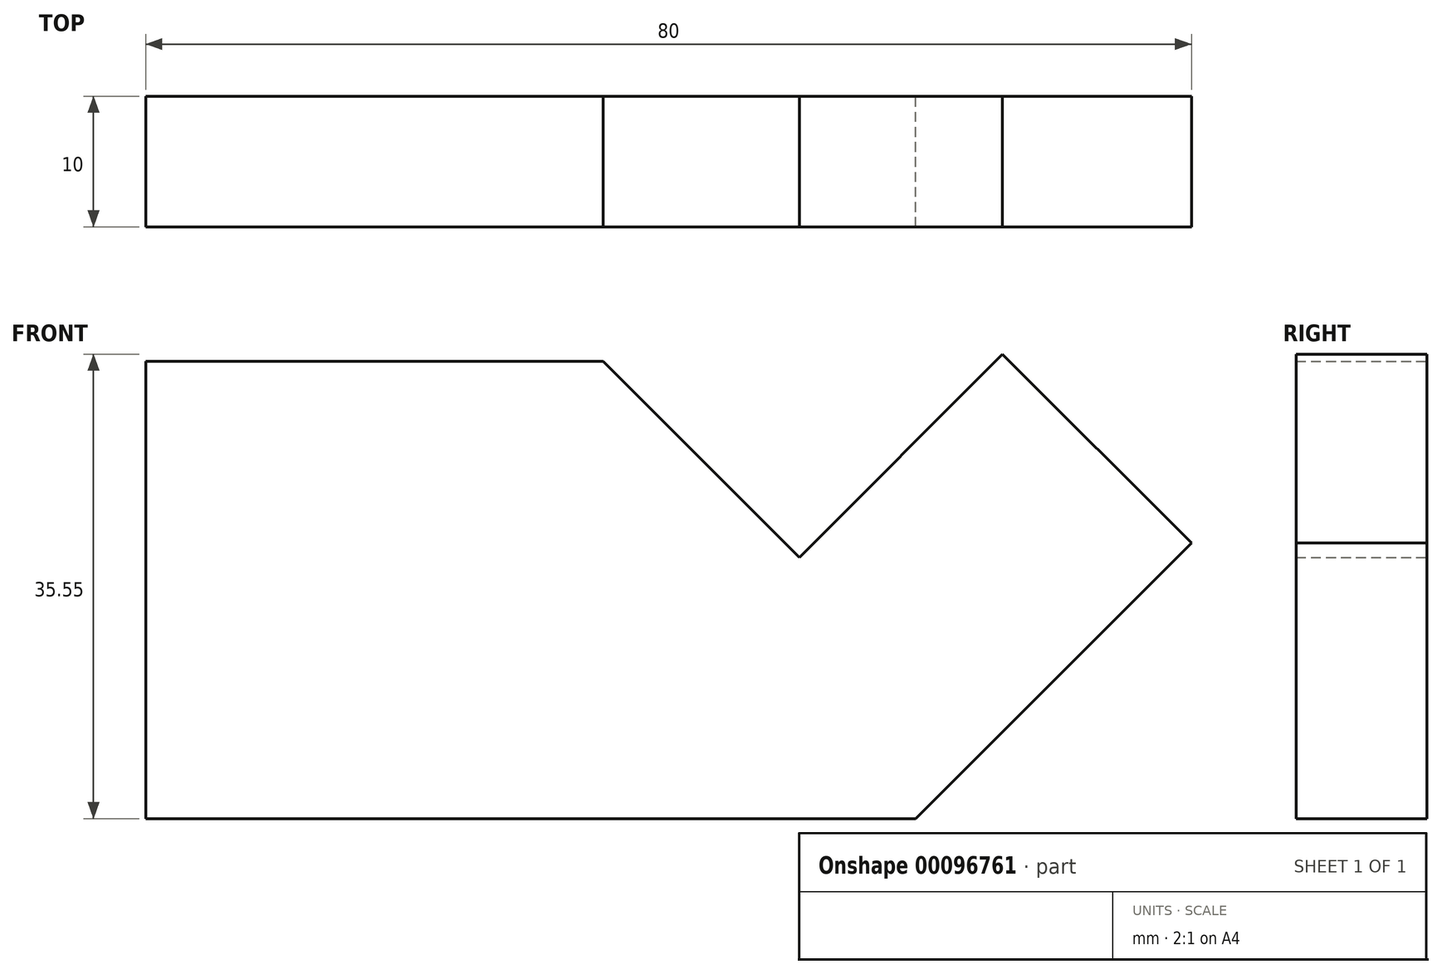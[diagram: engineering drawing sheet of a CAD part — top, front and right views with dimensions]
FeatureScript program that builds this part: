
annotation { "Feature Type Name" : "Feature", "Feature Type Description" : "" }
export const myFeature = defineFeature(function(context is Context, id is Id, definition is map)
    precondition{}
    {
        {
            var Q0;
            Q0=qCreatedBy(makeId("Front.planeOp"),FACE);
            var sketch = newSketch(context, id + "F0", { "sketchPlane" : qUnion([Q0])});
            skLineSegment(sketch, "E0", {"start": v(0, 0) * mm, "end": v(0, 35) * mm});
            skLineSegment(sketch, "E1", {"start": v(0, 35) * mm, "end": v(35, 35) * mm});
            skLineSegment(sketch, "E2", {"start": v(35, 35) * mm, "end": v(50, 20) * mm});
            skLineSegment(sketch, "E3", {"start": v(50, 20) * mm, "end": v(65.55, 35.55) * mm});
            skLineSegment(sketch, "E4", {"start": v(65.55, 35.55) * mm, "end": v(80, 21.1) * mm});
            skLineSegment(sketch, "E5", {"start": v(80, 21.1) * mm, "end": v(58.9, 0) * mm});
            skLineSegment(sketch, "E6", {"start": v(0, 0) * mm, "end": v(58.9, 0) * mm});
            skSolve(sketch);
        }
        {
            var Q0;
            Q0=makeQuery(id+"F0.imprint","IMPRINT",FACE,{"disambiguationData":[TD([[makeQuery(id+"F0.imprint","IMPRINT",EDGE,{"derivedFrom":sQuery(id+"F0.wireOp",EDGE,"E0")}),-1.0]])]});
            extrude(context, id + "F1", {"entities" : qUnion([Q0]), "depth" : 10 * mm});
        }
    });
